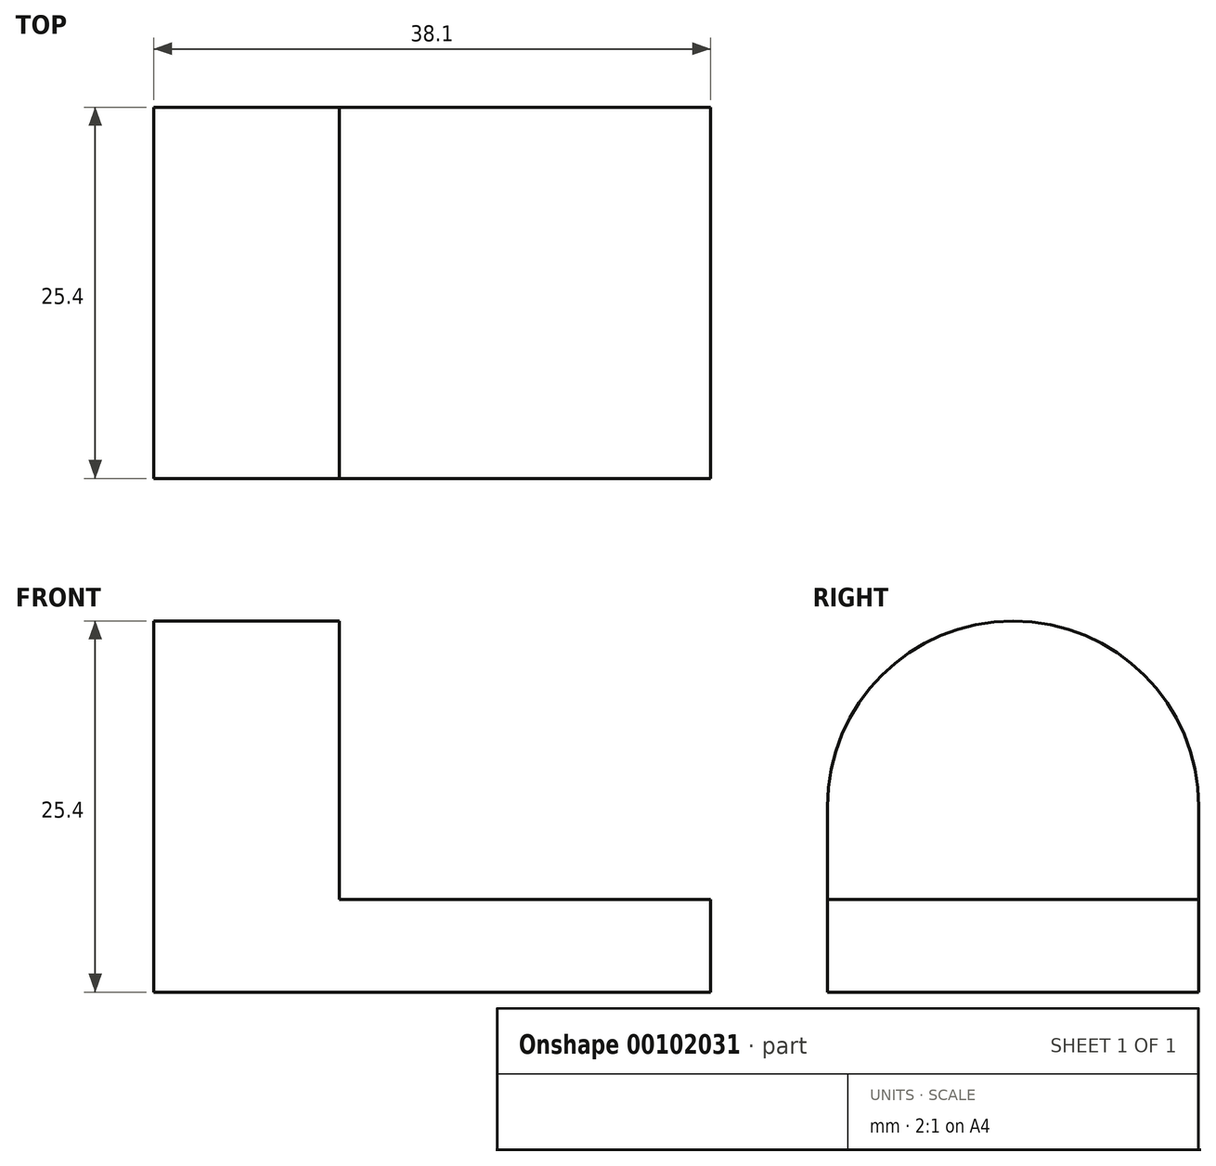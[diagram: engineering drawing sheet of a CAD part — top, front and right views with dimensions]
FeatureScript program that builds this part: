
annotation { "Feature Type Name" : "Feature", "Feature Type Description" : "" }
export const myFeature = defineFeature(function(context is Context, id is Id, definition is map)
    precondition{}
    {
        {
            var Q0;
            Q0=qCreatedBy(makeId("Front.planeOp"),FACE);
            var sketch = newSketch(context, id + "F0", { "sketchPlane" : qUnion([Q0])});
            skLineSegment(sketch, "E0", {"start": v(0, 0) * mm, "end": v(0, 25.4) * mm});
            skLineSegment(sketch, "E1", {"start": v(0, 25.4) * mm, "end": v(12.7, 25.4) * mm});
            skLineSegment(sketch, "E2", {"start": v(12.7, 25.4) * mm, "end": v(12.7, 0) * mm});
            skLineSegment(sketch, "E3", {"start": v(12.7, 0) * mm, "end": v(0, 0) * mm});
            skSolve(sketch);
        }
        {
            var Q0;
            Q0 = qSketchRegion(id + "F0", true);
            extrude(context, id + "F1", {"entities" : qUnion([Q0]), "oppositeDirection" : true, "depth" : 25.4 * mm});
        }
        {
            var Q0;
            Q0=qCreatedBy(makeId("Right.planeOp"),FACE);
            var sketch = newSketch(context, id + "F2", { "sketchPlane" : qUnion([Q0])});
            skLineSegment(sketch, "E4", {"start": v(0, 6.35) * mm, "end": v(0, 12.7) * mm});
            skLineSegment(sketch, "E5", {"start": v(25.4, 6.35) * mm, "end": v(25.4, 12.7) * mm});
            skLineSegment(sketch, "E6", {"start": v(0, 6.35) * mm, "end": v(25.4, 6.35) * mm});
            skArc(sketch, "E7", {"start": v(0, 12.7) * mm, "mid": v(12.7, 25.4) * mm, "end": v(25.4, 12.7) * mm});
            skSolve(sketch);
        }
        {
            var Q0;
            Q0 = qSketchRegion(id + "F2", true);
            extrude(context, id + "F3", {"entities" : qUnion([Q0]), "operationType" : NewBodyOperationType.INTERSECT, "depth" : 12.7 * mm});
        }
        {
            var Q0;
            Q0=qCreatedBy(makeId("Front.planeOp"),FACE);
            var sketch = newSketch(context, id + "F4", { "sketchPlane" : qUnion([Q0])});
            skLineSegment(sketch, "E8", {"start": v(0, 0) * mm, "end": v(0, 6.35) * mm});
            skLineSegment(sketch, "E9", {"start": v(0, 6.35) * mm, "end": v(38.1, 6.35) * mm});
            skLineSegment(sketch, "E10", {"start": v(38.1, 6.35) * mm, "end": v(38.1, 0) * mm});
            skLineSegment(sketch, "E11", {"start": v(38.1, 0) * mm, "end": v(0, 0) * mm});
            skSolve(sketch);
        }
        {
            var Q0;
            Q0 = qSketchRegion(id + "F4", true);
            extrude(context, id + "F5", {"entities" : qUnion([Q0]), "operationType" : NewBodyOperationType.ADD, "oppositeDirection" : true, "depth" : 25.4 * mm});
        }
    });
